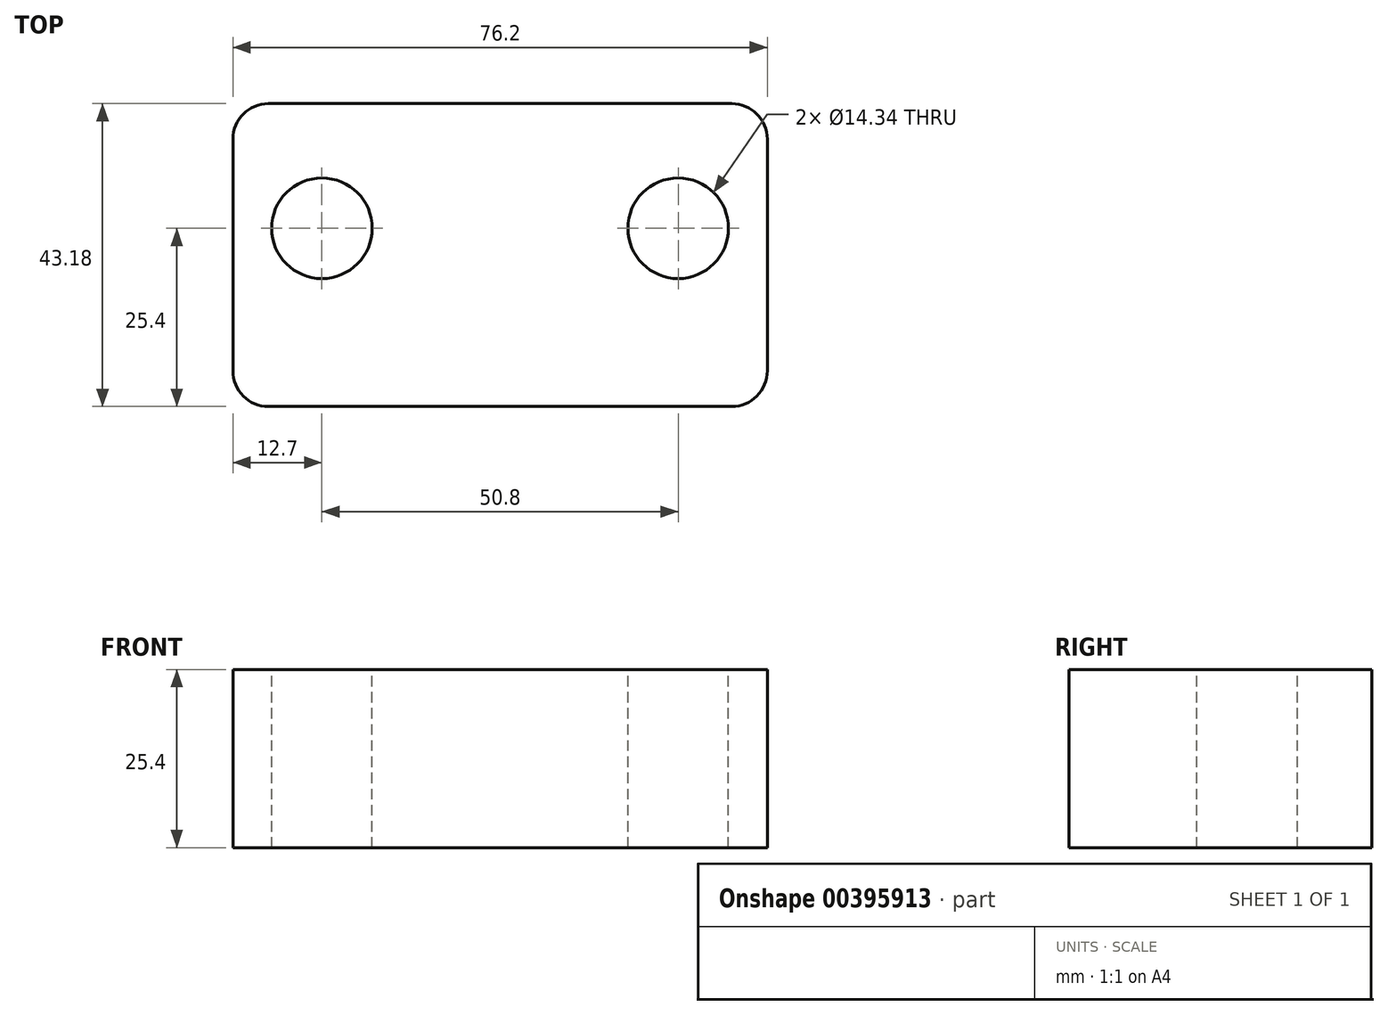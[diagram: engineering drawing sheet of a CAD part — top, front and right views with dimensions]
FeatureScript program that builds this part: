
annotation { "Feature Type Name" : "Feature", "Feature Type Description" : "" }
export const myFeature = defineFeature(function(context is Context, id is Id, definition is map)
    precondition{}
    {
        {
            var Q0;
            Q0=qCreatedBy(makeId("Top.planeOp"),FACE);
            var sketch = newSketch(context, id + "F0", { "sketchPlane" : qUnion([Q0])});
            skLineSegment(sketch, "E0", {"start": v(0, 0) * mm, "end": v(-33.02, 0) * mm});
            skLineSegment(sketch, "E1", {"start": v(-38.1, 5.08) * mm, "end": v(-38.1, 38.1) * mm});
            skLineSegment(sketch, "E2", {"start": v(-33.02, 43.18) * mm, "end": v(33.02, 43.18) * mm});
            skLineSegment(sketch, "E3", {"start": v(38.1, 38.1) * mm, "end": v(38.1, 5.08) * mm});
            skLineSegment(sketch, "E4", {"start": v(33.02, 0) * mm, "end": v(0, 0) * mm});
            skPoint(sketch, "E5.visualSharp", {"position": v(-38.1, 43.18) * mm});
            skArc(sketch, "E5.filletArc", {"start": v(-33.02, 43.18) * mm, "mid": v(-36.61, 41.7) * mm, "end": v(-38.1, 38.1) * mm});
            skPoint(sketch, "E6.visualSharp", {"position": v(38.1, 43.18) * mm});
            skArc(sketch, "E6.filletArc", {"start": v(38.1, 38.1) * mm, "mid": v(36.61, 41.7) * mm, "end": v(33.02, 43.18) * mm});
            skPoint(sketch, "E7.visualSharp", {"position": v(38.1, 0) * mm});
            skArc(sketch, "E7.filletArc", {"start": v(33.02, 0) * mm, "mid": v(36.61, 1.49) * mm, "end": v(38.1, 5.08) * mm});
            skPoint(sketch, "E8.visualSharp", {"position": v(-38.1, 0) * mm});
            skArc(sketch, "E8.filletArc", {"start": v(-38.1, 5.08) * mm, "mid": v(-36.61, 1.49) * mm, "end": v(-33.02, 0) * mm});
            skSolve(sketch);
        }
        {
            var Q0;
            Q0 = qSketchRegion(id + "F0", true);
            extrude(context, id + "F1", {"entities" : qUnion([Q0]), "depth" : 50.8 * mm});
        }
        {
            var Q0;
            Q0=makeQuery(id+"F1.opExtrude","CAP_FACE",FACE,{"disambiguationData":[OSD([sQuery(id+"F0.wireOp",EDGE,"E0"),sQuery(id+"F0.wireOp",EDGE,"E1"),sQuery(id+"F0.wireOp",EDGE,"E2"),sQuery(id+"F0.wireOp",EDGE,"E3"),sQuery(id+"F0.wireOp",EDGE,"E4"),sQuery(id+"F0.wireOp",EDGE,"E5.filletArc"),sQuery(id+"F0.wireOp",EDGE,"E6.filletArc"),sQuery(id+"F0.wireOp",EDGE,"E7.filletArc"),sQuery(id+"F0.wireOp",EDGE,"E8.filletArc")])],"isStart":false});
            var sketch = newSketch(context, id + "F2", { "sketchPlane" : qUnion([Q0])});
            skCircle(sketch, "E9", {"center": v(-25.4, 25.4) * mm, "radius": 7.17 * mm});
            skCircle(sketch, "E10.MirrorC", {"center": v(25.4, 25.4) * mm, "radius": 7.17 * mm});
            skSolve(sketch);
        }
        {
            var Q0;
            Q0 = qSketchRegion(id + "F2", true);
            var Q1;
            Q1=makeQuery(id+"F1.opExtrude","CAP_FACE",FACE,{"disambiguationData":[OSD([sQuery(id+"F0.wireOp",EDGE,"E0"),sQuery(id+"F0.wireOp",EDGE,"E1"),sQuery(id+"F0.wireOp",EDGE,"E2"),sQuery(id+"F0.wireOp",EDGE,"E3"),sQuery(id+"F0.wireOp",EDGE,"E4"),sQuery(id+"F0.wireOp",EDGE,"E5.filletArc"),sQuery(id+"F0.wireOp",EDGE,"E6.filletArc"),sQuery(id+"F0.wireOp",EDGE,"E7.filletArc"),sQuery(id+"F0.wireOp",EDGE,"E8.filletArc")])],"isStart":true});
            extrude(context, id + "F3", {"entities" : qUnion([Q0, Q1]), "operationType" : NewBodyOperationType.REMOVE, "oppositeDirection" : true, "depth" : 54.6 * mm, "hasSecondDirection" : true, "secondDirectionOppositeDirection" : false, "secondDirectionDepth" : 25.4 * mm});
        }
    });
